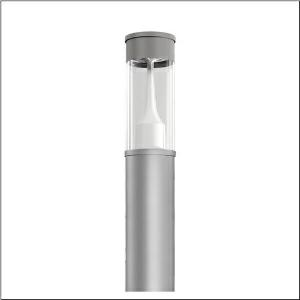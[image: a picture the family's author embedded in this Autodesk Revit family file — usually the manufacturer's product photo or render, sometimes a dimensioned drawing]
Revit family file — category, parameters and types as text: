
# Revit family: city-light_400_iq___st1_2a_5xa5305kf14hp_bbb3
name_source: partatom
category: Lighting Fixtures
units: mm (PartAtom-declared; Revit-internal decimal feet)

## family parameters
Cut with Voids When Loaded = No
Host = Face
Light Source = No
Part Type = Normal
Room Calculation Point = No
Round Connector Dimension = Use Diameter
Shared = No

## types (1)
- --- (1 x LED, 4940 lm, 33.6 W, 4000K)
    Apparent Load = 34 VA
    CIE Flux Codes = 22 61 94 96 100
    Color Rendering = 70
    Color Temperature = 4000K
    Default Elevation = 1800 mm
    Description = City-Light 400 iQ, light pillar, Module 540 iQ-SR, primary light control with 3 zone facetted reflector, of plastic, silver coated, highly specular, structured, primary optical cover: cover, of PMMA, transparent, partly coated, light distribution: ST1.2a, primary light characteristic: asymmetric, LED, High Power LED, rated luminous flux: 4.940lm, luminous efficacy: 147lm/W, light colour: 740, colour temperature: 4000K, control gear: ECG iQ, control: presetting dimming logarithmic, Street-Remote, Auto-Match, Temp-Guard, Lumen-Switch, Night-Set, Smart-Wire, Light-Fading, Desk-Remote (wireless, voltage-free reading and setting of iQ features in the workshop via application-optimized NFC function/RFID function), optimised constant luminous flux control (CLO 2.0), with terminal, 6-pole, max. 2.5mm², mains connection: 230..240V, AC, 50/60Hz, start of lifetime: 34W, end of service life: 36W, reduction: 15W, luminaire housing, cylindrical, of extruded aluminium section, coated, Siteco® metallic grey (DB 702S), length: 4.694mm, diameter: 200mm, Module 540 iQ-SR, traffic white (RAL 9016), equipment: Power, protection rating (complete): IP65, insulation class (complete): insulation class II (safety insulation), certification: CE, ENEC, VDE, packaging unit: 1 piece

Light Distribution: ST1.2a
    Height = 500 mm
    Lamp = 1 x LED
    Lamp Light Flux = 4940 lm
    Lamp Power = 33.6 W
    Lamp count = 1
    Length = 200 mm  [stored 0.656168 ft]
    Luminous efficacy = 147 lm/W
    Manufacturer = Siteco
    ModVariant = No
    Model = 5XA5305KF14HP
    Mounting Place = Floor
    Mounting Type = Freestanding
    Number of Poles = 1
    OnlyDefault = Yes
    Power Factor = 1
    Product Name = City-Light 400 iQ | ST1.2a
    Product group = light pillar
    ProductGroupID = 1303
    Protection Class = Protection class II
    Protection Degree = IP 65
    RLX_Detail_Level = 1
    RLX_Emergency_Light_Flux = 0 lm
    RLX_Emergency_Type = 0
    RLX_Emergency_Type_DB = No
    RlxData = <blob elided: 53453 chars, md5=2a1d631f>
    Socket = socket
    Standby Power = 0 W
    System Light Flux = 4940 lm
    System Power = 34 W
    Type Comments = factory setting: luminous flux: 100 % | dim-lin: 254 | 695 mA
    Type Image = l_1006916.jpg
    URL = http://relux.com
    VarID = @adj_127259
    Voltage = 0 V
    Weight = 0.00 kg
    Width = 0 mm  [stored 0 ft]

note: [stored X ft] marks values corroborated as IEEE doubles in the binary element streams (Revit-internal decimal feet)

## geometry (parser evidence)
native form markers: Blend x4, Sweep x11
no freeform markers — native parametric forms only
